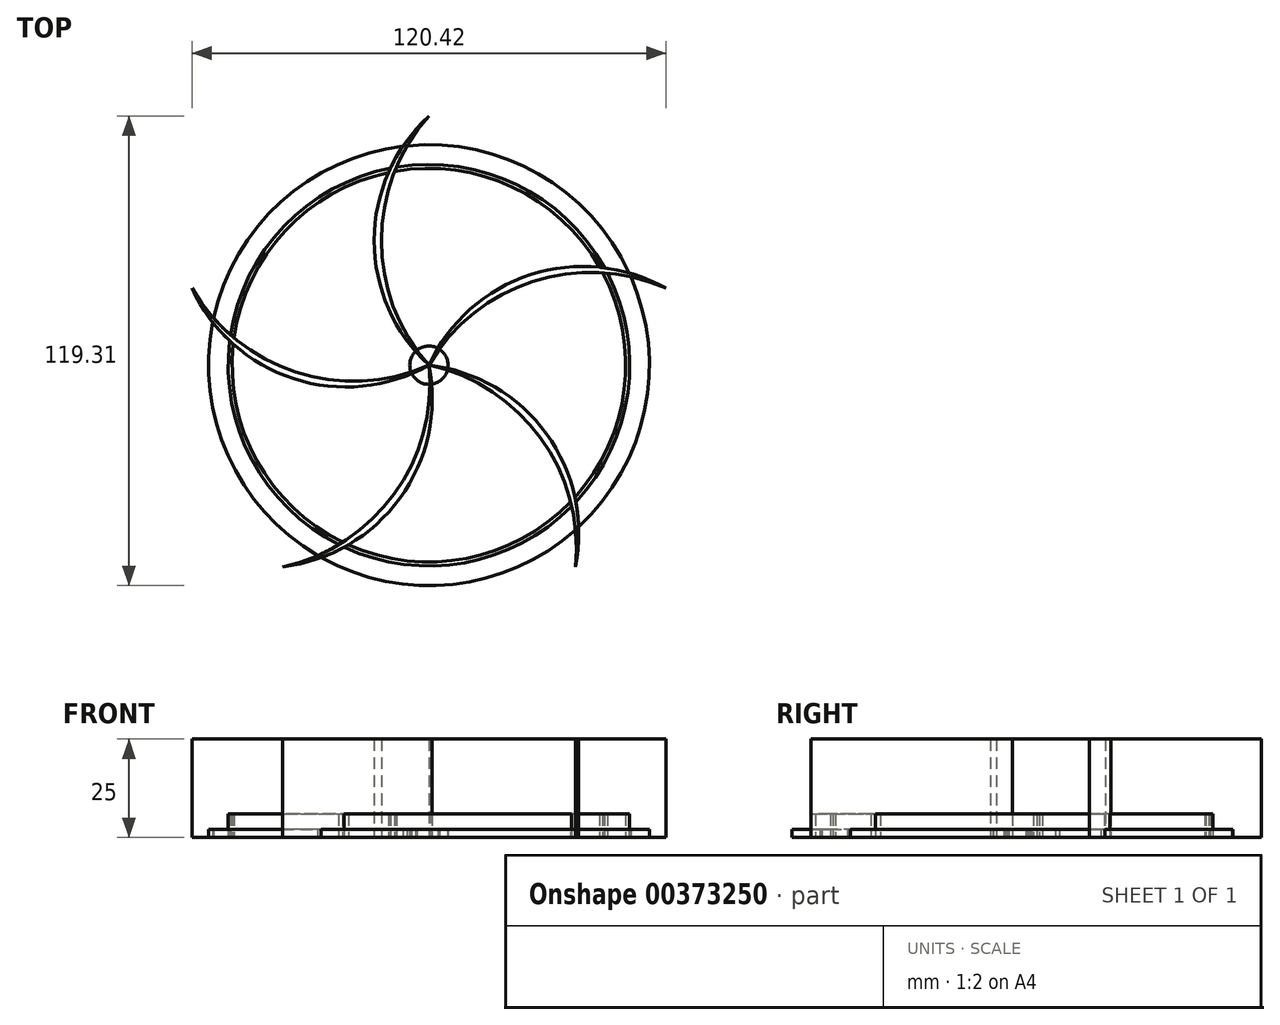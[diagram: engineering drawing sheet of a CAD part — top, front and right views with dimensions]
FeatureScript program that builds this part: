
annotation { "Feature Type Name" : "Feature", "Feature Type Description" : "" }
export const myFeature = defineFeature(function(context is Context, id is Id, definition is map)
    precondition{}
    {
        {
            var Q0;
            Q0=qCreatedBy(makeId("Top.planeOp"),FACE);
            var sketch = newSketch(context, id + "F0", { "sketchPlane" : qUnion([Q0])});
            skCircle(sketch, "E0", {"center": v(0, 0) * mm, "radius": 50 * mm});
            skArc(sketch, "E1", {"start": v(0, 63.3) * mm, "mid": v(-13.9, 31.65) * mm, "end": v(0, 0) * mm});
            skArc(sketch, "E2.1.0", {"start": v(-60.2, 19.56) * mm, "mid": v(-34.4, -3.43) * mm, "end": v(0, 0) * mm});
            skArc(sketch, "E2.2.0", {"start": v(-37.2, -51.22) * mm, "mid": v(-7.36, -33.78) * mm, "end": v(0, 0) * mm});
            skArc(sketch, "E2.3.0", {"start": v(37.2, -51.22) * mm, "mid": v(29.85, -17.44) * mm, "end": v(0, 0) * mm});
            skArc(sketch, "E2.4.0", {"start": v(60.2, 19.56) * mm, "mid": v(25.8, 23) * mm, "end": v(0, 0) * mm});
            skArc(sketch, "E3", {"start": v(0, 63.3) * mm, "mid": v(-12.09, 31.65) * mm, "end": v(0, 0) * mm});
            skArc(sketch, "E4.1.0", {"start": v(-60.2, 19.56) * mm, "mid": v(-33.84, -1.72) * mm, "end": v(0, 0) * mm});
            skArc(sketch, "E4.2.0", {"start": v(-37.2, -51.22) * mm, "mid": v(-8.82, -32.71) * mm, "end": v(0, 0) * mm});
            skArc(sketch, "E4.3.0", {"start": v(37.2, -51.22) * mm, "mid": v(28.39, -18.5) * mm, "end": v(0, 0) * mm});
            skArc(sketch, "E4.4.0", {"start": v(60.2, 19.56) * mm, "mid": v(26.37, 21.28) * mm, "end": v(0, 0) * mm});
            skCircle(sketch, "E5.0", {"center": v(0, 0) * mm, "radius": 51 * mm});
            skCircle(sketch, "E6.0", {"center": v(0, 0) * mm, "radius": 56 * mm});
            skCircle(sketch, "E7", {"center": v(0, 0) * mm, "radius": 4.87 * mm});
            skSolve(sketch);
        }
        {
            var Q0;
            {var subQ0=sQuery(id+"F0.wireOp",EDGE,"E2.1.0");var subQ1=sQuery(id+"F0.wireOp",EDGE,"E0");var subQ2=makeQuery(id+"F0.imprint","INTERSECT",VERTEX,{"derivedFrom":[subQ1,subQ0]});Q0=makeQuery(id+"F0.imprint","IMPRINT",FACE,{"disambiguationData":[TD([[makeQuery(id+"F0.imprint","IMPRINT",EDGE,{"disambiguationData":[TD([[subQ2,-1.0]])],"derivedFrom":subQ1}),-1.0]])]});}
            var Q1;
            {var subQ0=sQuery(id+"F0.wireOp",EDGE,"E1");var subQ1=sQuery(id+"F0.wireOp",EDGE,"E0");var subQ2=makeQuery(id+"F0.imprint","INTERSECT",VERTEX,{"derivedFrom":[subQ1,subQ0]});Q1=makeQuery(id+"F0.imprint","IMPRINT",FACE,{"disambiguationData":[TD([[makeQuery(id+"F0.imprint","IMPRINT",EDGE,{"disambiguationData":[TD([[subQ2,-1.0]])],"derivedFrom":subQ1}),-1.0]])]});}
            var Q2;
            {var subQ0=sQuery(id+"F0.wireOp",EDGE,"E2.4.0");var subQ1=sQuery(id+"F0.wireOp",EDGE,"E0");var subQ2=makeQuery(id+"F0.imprint","INTERSECT",VERTEX,{"derivedFrom":[subQ1,subQ0]});Q2=makeQuery(id+"F0.imprint","IMPRINT",FACE,{"disambiguationData":[TD([[makeQuery(id+"F0.imprint","IMPRINT",EDGE,{"disambiguationData":[TD([[subQ2,-1.0]])],"derivedFrom":subQ1}),-1.0]])]});}
            var Q3;
            {var subQ0=sQuery(id+"F0.wireOp",EDGE,"E4.4.0");var subQ1=sQuery(id+"F0.wireOp",EDGE,"E0");var subQ2=makeQuery(id+"F0.imprint","INTERSECT",VERTEX,{"derivedFrom":[subQ1,subQ0]});Q3=makeQuery(id+"F0.imprint","IMPRINT",FACE,{"disambiguationData":[TD([[makeQuery(id+"F0.imprint","IMPRINT",EDGE,{"disambiguationData":[TD([[subQ2,1.0]])],"derivedFrom":subQ1}),-1.0]])]});}
            var Q4;
            {var subQ0=sQuery(id+"F0.wireOp",EDGE,"E2.2.0");var subQ1=sQuery(id+"F0.wireOp",EDGE,"E0");var subQ2=makeQuery(id+"F0.imprint","INTERSECT",VERTEX,{"derivedFrom":[subQ1,subQ0]});Q4=makeQuery(id+"F0.imprint","IMPRINT",FACE,{"disambiguationData":[TD([[makeQuery(id+"F0.imprint","IMPRINT",EDGE,{"disambiguationData":[TD([[subQ2,-1.0]])],"derivedFrom":subQ1}),-1.0]])]});}
            extrude(context, id + "F1", {"entities" : qUnion([Q0, Q1, Q2, Q3, Q4]), "depth" : 6 * mm});
        }
        {
            var Q0;
            {var subQ0=sQuery(id+"F0.wireOp",EDGE,"E4.2.0");var subQ1=sQuery(id+"F0.wireOp",EDGE,"E0");var subQ2=makeQuery(id+"F0.imprint","INTERSECT",VERTEX,{"derivedFrom":[subQ1,subQ0]});Q0=makeQuery(id+"F0.imprint","IMPRINT",FACE,{"disambiguationData":[TD([[makeQuery(id+"F0.imprint","IMPRINT",EDGE,{"disambiguationData":[TD([[subQ2,-1.0]])],"derivedFrom":subQ1}),1.0]])]});}
            var Q1;
            {var subQ0=sQuery(id+"F0.wireOp",EDGE,"E4.3.0");var subQ1=sQuery(id+"F0.wireOp",EDGE,"E0");var subQ2=makeQuery(id+"F0.imprint","INTERSECT",VERTEX,{"derivedFrom":[subQ1,subQ0]});Q1=makeQuery(id+"F0.imprint","IMPRINT",FACE,{"disambiguationData":[TD([[makeQuery(id+"F0.imprint","IMPRINT",EDGE,{"disambiguationData":[TD([[subQ2,-1.0]])],"derivedFrom":subQ1}),1.0]])]});}
            var Q2;
            {var subQ0=sQuery(id+"F0.wireOp",EDGE,"E2.4.0");var subQ1=sQuery(id+"F0.wireOp",EDGE,"E0");var subQ2=makeQuery(id+"F0.imprint","INTERSECT",VERTEX,{"derivedFrom":[subQ1,subQ0]});Q2=makeQuery(id+"F0.imprint","IMPRINT",FACE,{"disambiguationData":[TD([[makeQuery(id+"F0.imprint","IMPRINT",EDGE,{"disambiguationData":[TD([[subQ2,1.0]])],"derivedFrom":subQ1}),1.0]])]});}
            var Q3;
            {var subQ0=sQuery(id+"F0.wireOp",EDGE,"E3");var subQ1=sQuery(id+"F0.wireOp",EDGE,"E0");var subQ2=makeQuery(id+"F0.imprint","INTERSECT",VERTEX,{"derivedFrom":[subQ1,subQ0]});Q3=makeQuery(id+"F0.imprint","IMPRINT",FACE,{"disambiguationData":[TD([[makeQuery(id+"F0.imprint","IMPRINT",EDGE,{"disambiguationData":[TD([[subQ2,-1.0]])],"derivedFrom":subQ1}),1.0]])]});}
            var Q4;
            {var subQ0=sQuery(id+"F0.wireOp",EDGE,"E4.1.0");var subQ1=sQuery(id+"F0.wireOp",EDGE,"E0");var subQ2=makeQuery(id+"F0.imprint","INTERSECT",VERTEX,{"derivedFrom":[subQ1,subQ0]});Q4=makeQuery(id+"F0.imprint","IMPRINT",FACE,{"disambiguationData":[TD([[makeQuery(id+"F0.imprint","IMPRINT",EDGE,{"disambiguationData":[TD([[subQ2,-1.0]])],"derivedFrom":subQ1}),1.0]])]});}
            var Q5;
            {var subQ0=sQuery(id+"F0.wireOp",EDGE,"E4.4.0");var subQ1=sQuery(id+"F0.wireOp",EDGE,"E2.4.0");var subQ2=makeQuery(id+"F0.imprint","INTERSECT",VERTEX,{"derivedFrom":[subQ1,subQ0]});Q5=makeQuery(id+"F0.imprint","IMPRINT",FACE,{"disambiguationData":[TD([[makeQuery(id+"F0.imprint","IMPRINT",EDGE,{"disambiguationData":[TD([[subQ2,-1.0]])],"derivedFrom":subQ1}),1.0]])]});}
            var Q6;
            {var subQ0=sQuery(id+"F0.wireOp",EDGE,"E2.4.0");var subQ1=sQuery(id+"F0.wireOp",EDGE,"E0");var subQ2=makeQuery(id+"F0.imprint","INTERSECT",VERTEX,{"derivedFrom":[subQ1,subQ0]});Q6=makeQuery(id+"F0.imprint","IMPRINT",FACE,{"disambiguationData":[TD([[makeQuery(id+"F0.imprint","IMPRINT",EDGE,{"disambiguationData":[TD([[subQ2,1.0]])],"derivedFrom":subQ1}),-1.0]])]});}
            var Q7;
            {var subQ0=sQuery(id+"F0.wireOp",EDGE,"E3");var subQ1=sQuery(id+"F0.wireOp",EDGE,"E0");var subQ2=makeQuery(id+"F0.imprint","INTERSECT",VERTEX,{"derivedFrom":[subQ1,subQ0]});Q7=makeQuery(id+"F0.imprint","IMPRINT",FACE,{"disambiguationData":[TD([[makeQuery(id+"F0.imprint","IMPRINT",EDGE,{"disambiguationData":[TD([[subQ2,-1.0]])],"derivedFrom":subQ1}),-1.0]])]});}
            var Q8;
            {var subQ0=sQuery(id+"F0.wireOp",EDGE,"E3");var subQ1=sQuery(id+"F0.wireOp",EDGE,"E1");var subQ2=makeQuery(id+"F0.imprint","INTERSECT",VERTEX,{"derivedFrom":[subQ1,subQ0]});Q8=makeQuery(id+"F0.imprint","IMPRINT",FACE,{"disambiguationData":[TD([[makeQuery(id+"F0.imprint","IMPRINT",EDGE,{"disambiguationData":[TD([[subQ2,-1.0]])],"derivedFrom":subQ1}),1.0]])]});}
            var Q9;
            {var subQ0=sQuery(id+"F0.wireOp",EDGE,"E4.1.0");var subQ1=sQuery(id+"F0.wireOp",EDGE,"E0");var subQ2=makeQuery(id+"F0.imprint","INTERSECT",VERTEX,{"derivedFrom":[subQ1,subQ0]});Q9=makeQuery(id+"F0.imprint","IMPRINT",FACE,{"disambiguationData":[TD([[makeQuery(id+"F0.imprint","IMPRINT",EDGE,{"disambiguationData":[TD([[subQ2,-1.0]])],"derivedFrom":subQ1}),-1.0]])]});}
            var Q10;
            {var subQ0=sQuery(id+"F0.wireOp",EDGE,"E4.1.0");var subQ1=sQuery(id+"F0.wireOp",EDGE,"E2.1.0");var subQ2=makeQuery(id+"F0.imprint","INTERSECT",VERTEX,{"derivedFrom":[subQ1,subQ0]});Q10=makeQuery(id+"F0.imprint","IMPRINT",FACE,{"disambiguationData":[TD([[makeQuery(id+"F0.imprint","IMPRINT",EDGE,{"disambiguationData":[TD([[subQ2,-1.0]])],"derivedFrom":subQ1}),1.0]])]});}
            var Q11;
            {var subQ0=sQuery(id+"F0.wireOp",EDGE,"E4.2.0");var subQ1=sQuery(id+"F0.wireOp",EDGE,"E0");var subQ2=makeQuery(id+"F0.imprint","INTERSECT",VERTEX,{"derivedFrom":[subQ1,subQ0]});Q11=makeQuery(id+"F0.imprint","IMPRINT",FACE,{"disambiguationData":[TD([[makeQuery(id+"F0.imprint","IMPRINT",EDGE,{"disambiguationData":[TD([[subQ2,-1.0]])],"derivedFrom":subQ1}),-1.0]])]});}
            var Q12;
            {var subQ0=sQuery(id+"F0.wireOp",EDGE,"E4.2.0");var subQ1=sQuery(id+"F0.wireOp",EDGE,"E2.2.0");var subQ2=makeQuery(id+"F0.imprint","INTERSECT",VERTEX,{"derivedFrom":[subQ1,subQ0]});Q12=makeQuery(id+"F0.imprint","IMPRINT",FACE,{"disambiguationData":[TD([[makeQuery(id+"F0.imprint","IMPRINT",EDGE,{"disambiguationData":[TD([[subQ2,-1.0]])],"derivedFrom":subQ1}),1.0]])]});}
            var Q13;
            {var subQ0=sQuery(id+"F0.wireOp",EDGE,"E4.3.0");var subQ1=sQuery(id+"F0.wireOp",EDGE,"E0");var subQ2=makeQuery(id+"F0.imprint","INTERSECT",VERTEX,{"derivedFrom":[subQ1,subQ0]});Q13=makeQuery(id+"F0.imprint","IMPRINT",FACE,{"disambiguationData":[TD([[makeQuery(id+"F0.imprint","IMPRINT",EDGE,{"disambiguationData":[TD([[subQ2,-1.0]])],"derivedFrom":subQ1}),-1.0]])]});}
            var Q14;
            {var subQ0=sQuery(id+"F0.wireOp",EDGE,"E4.3.0");var subQ1=sQuery(id+"F0.wireOp",EDGE,"E2.3.0");var subQ2=makeQuery(id+"F0.imprint","INTERSECT",VERTEX,{"derivedFrom":[subQ1,subQ0]});Q14=makeQuery(id+"F0.imprint","IMPRINT",FACE,{"disambiguationData":[TD([[makeQuery(id+"F0.imprint","IMPRINT",EDGE,{"disambiguationData":[TD([[subQ2,-1.0]])],"derivedFrom":subQ1}),1.0]])]});}
            var Q15;
            {var subQ0=sQuery(id+"F0.wireOp",EDGE,"E6.0");var subQ1=sQuery(id+"F0.wireOp",EDGE,"E2.1.0");var subQ2=makeQuery(id+"F0.imprint","INTERSECT",VERTEX,{"derivedFrom":[subQ1,subQ0]});Q15=makeQuery(id+"F0.imprint","IMPRINT",FACE,{"disambiguationData":[TD([[makeQuery(id+"F0.imprint","IMPRINT",EDGE,{"disambiguationData":[TD([[subQ2,-1.0]])],"derivedFrom":subQ1}),1.0]])]});}
            var Q16;
            {var subQ0=sQuery(id+"F0.wireOp",EDGE,"E6.0");var subQ1=sQuery(id+"F0.wireOp",EDGE,"E2.2.0");var subQ2=makeQuery(id+"F0.imprint","INTERSECT",VERTEX,{"derivedFrom":[subQ1,subQ0]});Q16=makeQuery(id+"F0.imprint","IMPRINT",FACE,{"disambiguationData":[TD([[makeQuery(id+"F0.imprint","IMPRINT",EDGE,{"disambiguationData":[TD([[subQ2,-1.0]])],"derivedFrom":subQ1}),1.0]])]});}
            var Q17;
            {var subQ0=sQuery(id+"F0.wireOp",EDGE,"E6.0");var subQ1=sQuery(id+"F0.wireOp",EDGE,"E2.3.0");var subQ2=makeQuery(id+"F0.imprint","INTERSECT",VERTEX,{"derivedFrom":[subQ1,subQ0]});Q17=makeQuery(id+"F0.imprint","IMPRINT",FACE,{"disambiguationData":[TD([[makeQuery(id+"F0.imprint","IMPRINT",EDGE,{"disambiguationData":[TD([[subQ2,-1.0]])],"derivedFrom":subQ1}),1.0]])]});}
            var Q18;
            {var subQ0=sQuery(id+"F0.wireOp",EDGE,"E6.0");var subQ1=sQuery(id+"F0.wireOp",EDGE,"E2.4.0");var subQ2=makeQuery(id+"F0.imprint","INTERSECT",VERTEX,{"derivedFrom":[subQ1,subQ0]});Q18=makeQuery(id+"F0.imprint","IMPRINT",FACE,{"disambiguationData":[TD([[makeQuery(id+"F0.imprint","IMPRINT",EDGE,{"disambiguationData":[TD([[subQ2,-1.0]])],"derivedFrom":subQ1}),1.0]])]});}
            var Q19;
            {var subQ0=sQuery(id+"F0.wireOp",EDGE,"E6.0");var subQ1=sQuery(id+"F0.wireOp",EDGE,"E1");var subQ2=makeQuery(id+"F0.imprint","INTERSECT",VERTEX,{"derivedFrom":[subQ1,subQ0]});Q19=makeQuery(id+"F0.imprint","IMPRINT",FACE,{"disambiguationData":[TD([[makeQuery(id+"F0.imprint","IMPRINT",EDGE,{"disambiguationData":[TD([[subQ2,-1.0]])],"derivedFrom":subQ1}),1.0]])]});}
            var Q20;
            {var subQ1=sQuery(id+"F0.wireOp",EDGE,"E2.3.0");var subQ3=sQuery(id+"F0.wireOp",EDGE,"E7");var subQ4=makeQuery(id+"F0.imprint","INTERSECT",VERTEX,{"derivedFrom":[subQ1,subQ3]});Q20=makeQuery(id+"F0.imprint","IMPRINT",FACE,{"disambiguationData":[TD([[makeQuery(id+"F0.imprint","IMPRINT",EDGE,{"disambiguationData":[TD([[subQ4,1.0]])],"derivedFrom":subQ3}),1.0]])]});}
            var Q21;
            {var subQ1=sQuery(id+"F0.wireOp",EDGE,"E2.4.0");var subQ3=sQuery(id+"F0.wireOp",EDGE,"E7");var subQ4=makeQuery(id+"F0.imprint","INTERSECT",VERTEX,{"derivedFrom":[subQ1,subQ3]});Q21=makeQuery(id+"F0.imprint","IMPRINT",FACE,{"disambiguationData":[TD([[makeQuery(id+"F0.imprint","IMPRINT",EDGE,{"disambiguationData":[TD([[subQ4,1.0]])],"derivedFrom":subQ3}),1.0]])]});}
            var Q22;
            {var subQ1=sQuery(id+"F0.wireOp",EDGE,"E1");var subQ3=sQuery(id+"F0.wireOp",EDGE,"E7");var subQ4=makeQuery(id+"F0.imprint","INTERSECT",VERTEX,{"derivedFrom":[subQ1,subQ3]});Q22=makeQuery(id+"F0.imprint","IMPRINT",FACE,{"disambiguationData":[TD([[makeQuery(id+"F0.imprint","IMPRINT",EDGE,{"disambiguationData":[TD([[subQ4,1.0]])],"derivedFrom":subQ3}),1.0]])]});}
            var Q23;
            {var subQ1=sQuery(id+"F0.wireOp",EDGE,"E2.1.0");var subQ3=sQuery(id+"F0.wireOp",EDGE,"E7");var subQ4=makeQuery(id+"F0.imprint","INTERSECT",VERTEX,{"derivedFrom":[subQ1,subQ3]});Q23=makeQuery(id+"F0.imprint","IMPRINT",FACE,{"disambiguationData":[TD([[makeQuery(id+"F0.imprint","IMPRINT",EDGE,{"disambiguationData":[TD([[subQ4,1.0]])],"derivedFrom":subQ3}),1.0]])]});}
            var Q24;
            {var subQ1=sQuery(id+"F0.wireOp",EDGE,"E2.2.0");var subQ3=sQuery(id+"F0.wireOp",EDGE,"E7");var subQ4=makeQuery(id+"F0.imprint","INTERSECT",VERTEX,{"derivedFrom":[subQ1,subQ3]});Q24=makeQuery(id+"F0.imprint","IMPRINT",FACE,{"disambiguationData":[TD([[makeQuery(id+"F0.imprint","IMPRINT",EDGE,{"disambiguationData":[TD([[subQ4,1.0]])],"derivedFrom":subQ3}),1.0]])]});}
            extrude(context, id + "F2", {"entities" : qUnion([Q0, Q1, Q2, Q3, Q4, Q5, Q6, Q7, Q8, Q9, Q10, Q11, Q12, Q13, Q14, Q15, Q16, Q17, Q18, Q19, Q20, Q21, Q22, Q23, Q24]), "depth" : 25 * mm});
        }
        {
            var Q0;
            {var subQ0=sQuery(id+"F0.wireOp",EDGE,"E6.0");var subQ1=sQuery(id+"F0.wireOp",EDGE,"E2.1.0");var subQ2=makeQuery(id+"F0.imprint","INTERSECT",VERTEX,{"derivedFrom":[subQ1,subQ0]});Q0=makeQuery(id+"F0.imprint","IMPRINT",FACE,{"disambiguationData":[TD([[makeQuery(id+"F0.imprint","IMPRINT",EDGE,{"disambiguationData":[TD([[subQ2,-1.0]])],"derivedFrom":subQ1}),-1.0]])]});}
            var Q1;
            {var subQ0=sQuery(id+"F0.wireOp",EDGE,"E6.0");var subQ1=sQuery(id+"F0.wireOp",EDGE,"E2.2.0");var subQ2=makeQuery(id+"F0.imprint","INTERSECT",VERTEX,{"derivedFrom":[subQ1,subQ0]});Q1=makeQuery(id+"F0.imprint","IMPRINT",FACE,{"disambiguationData":[TD([[makeQuery(id+"F0.imprint","IMPRINT",EDGE,{"disambiguationData":[TD([[subQ2,-1.0]])],"derivedFrom":subQ1}),-1.0]])]});}
            var Q2;
            {var subQ0=sQuery(id+"F0.wireOp",EDGE,"E6.0");var subQ1=sQuery(id+"F0.wireOp",EDGE,"E1");var subQ2=makeQuery(id+"F0.imprint","INTERSECT",VERTEX,{"derivedFrom":[subQ1,subQ0]});Q2=makeQuery(id+"F0.imprint","IMPRINT",FACE,{"disambiguationData":[TD([[makeQuery(id+"F0.imprint","IMPRINT",EDGE,{"disambiguationData":[TD([[subQ2,-1.0]])],"derivedFrom":subQ1}),-1.0]])]});}
            var Q3;
            {var subQ0=sQuery(id+"F0.wireOp",EDGE,"E6.0");var subQ1=sQuery(id+"F0.wireOp",EDGE,"E2.4.0");var subQ2=makeQuery(id+"F0.imprint","INTERSECT",VERTEX,{"derivedFrom":[subQ1,subQ0]});Q3=makeQuery(id+"F0.imprint","IMPRINT",FACE,{"disambiguationData":[TD([[makeQuery(id+"F0.imprint","IMPRINT",EDGE,{"disambiguationData":[TD([[subQ2,-1.0]])],"derivedFrom":subQ1}),-1.0]])]});}
            var Q4;
            {var subQ0=sQuery(id+"F0.wireOp",EDGE,"E6.0");var subQ1=sQuery(id+"F0.wireOp",EDGE,"E2.3.0");var subQ2=makeQuery(id+"F0.imprint","INTERSECT",VERTEX,{"derivedFrom":[subQ1,subQ0]});Q4=makeQuery(id+"F0.imprint","IMPRINT",FACE,{"disambiguationData":[TD([[makeQuery(id+"F0.imprint","IMPRINT",EDGE,{"disambiguationData":[TD([[subQ2,-1.0]])],"derivedFrom":subQ1}),-1.0]])]});}
            var Q5;
            {var subQ1=sQuery(id+"F0.wireOp",EDGE,"E2.1.0");var subQ3=sQuery(id+"F0.wireOp",EDGE,"E7");var subQ4=makeQuery(id+"F0.imprint","INTERSECT",VERTEX,{"derivedFrom":[subQ1,subQ3]});Q5=makeQuery(id+"F0.imprint","IMPRINT",FACE,{"disambiguationData":[TD([[makeQuery(id+"F0.imprint","IMPRINT",EDGE,{"disambiguationData":[TD([[subQ4,-1.0]])],"derivedFrom":subQ3}),1.0]])]});}
            var Q6;
            {var subQ1=sQuery(id+"F0.wireOp",EDGE,"E2.2.0");var subQ3=sQuery(id+"F0.wireOp",EDGE,"E7");var subQ4=makeQuery(id+"F0.imprint","INTERSECT",VERTEX,{"derivedFrom":[subQ1,subQ3]});Q6=makeQuery(id+"F0.imprint","IMPRINT",FACE,{"disambiguationData":[TD([[makeQuery(id+"F0.imprint","IMPRINT",EDGE,{"disambiguationData":[TD([[subQ4,-1.0]])],"derivedFrom":subQ3}),1.0]])]});}
            var Q7;
            {var subQ1=sQuery(id+"F0.wireOp",EDGE,"E2.3.0");var subQ3=sQuery(id+"F0.wireOp",EDGE,"E7");var subQ4=makeQuery(id+"F0.imprint","INTERSECT",VERTEX,{"derivedFrom":[subQ1,subQ3]});Q7=makeQuery(id+"F0.imprint","IMPRINT",FACE,{"disambiguationData":[TD([[makeQuery(id+"F0.imprint","IMPRINT",EDGE,{"disambiguationData":[TD([[subQ4,-1.0]])],"derivedFrom":subQ3}),1.0]])]});}
            var Q8;
            {var subQ1=sQuery(id+"F0.wireOp",EDGE,"E2.4.0");var subQ3=sQuery(id+"F0.wireOp",EDGE,"E7");var subQ4=makeQuery(id+"F0.imprint","INTERSECT",VERTEX,{"derivedFrom":[subQ1,subQ3]});Q8=makeQuery(id+"F0.imprint","IMPRINT",FACE,{"disambiguationData":[TD([[makeQuery(id+"F0.imprint","IMPRINT",EDGE,{"disambiguationData":[TD([[subQ4,-1.0]])],"derivedFrom":subQ3}),1.0]])]});}
            var Q9;
            {var subQ1=sQuery(id+"F0.wireOp",EDGE,"E1");var subQ3=sQuery(id+"F0.wireOp",EDGE,"E7");var subQ4=makeQuery(id+"F0.imprint","INTERSECT",VERTEX,{"derivedFrom":[subQ1,subQ3]});Q9=makeQuery(id+"F0.imprint","IMPRINT",FACE,{"disambiguationData":[TD([[makeQuery(id+"F0.imprint","IMPRINT",EDGE,{"disambiguationData":[TD([[subQ4,-1.0]])],"derivedFrom":subQ3}),1.0]])]});}
            extrude(context, id + "F3", {"entities" : qUnion([Q0, Q1, Q2, Q3, Q4, Q5, Q6, Q7, Q8, Q9]), "depth" : 2 * mm});
        }
    });
